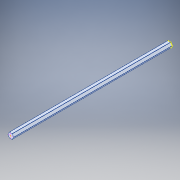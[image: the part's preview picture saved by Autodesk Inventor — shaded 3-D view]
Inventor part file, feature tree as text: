
AUTODESK INVENTOR PART (.ipt)
format: ipt  version: 2017 (Build 210142000, 142)  size: 158,720 bytes
history: native  units: in
note: dims shown in document units (in); Inventor stores cm internally (conversion verified against a paired STEP export)
features: sketch x7, split x1, projected_geometry x1, fillet x1
ambient origin geometry x8: Origin, YZ Plane, XZ Plane, XY Plane, X Axis, Y Axis, Z Axis, Center Point
bodies: Solid1 (feature_tree)
feature tree (10):
  sketch  "Sketch1"  dims[d11=16.0in]
  split  "Split1"
  sketch  "Sketch3"  dims[d13=7.8125in]
  sketch  "Sketch4"  dims[d14=3.5453in]
  sketch  "Sketch5"  dims[d15=3.5453in]
  sketch  "Sketch7"
  sketch  "Sketch8"
  sketch  "Sketch2"  dims[d12=7.8125in]
  projected_geometry  "Projected Loop1"
  fillet  "Fillet1"  Radius=8.5in
